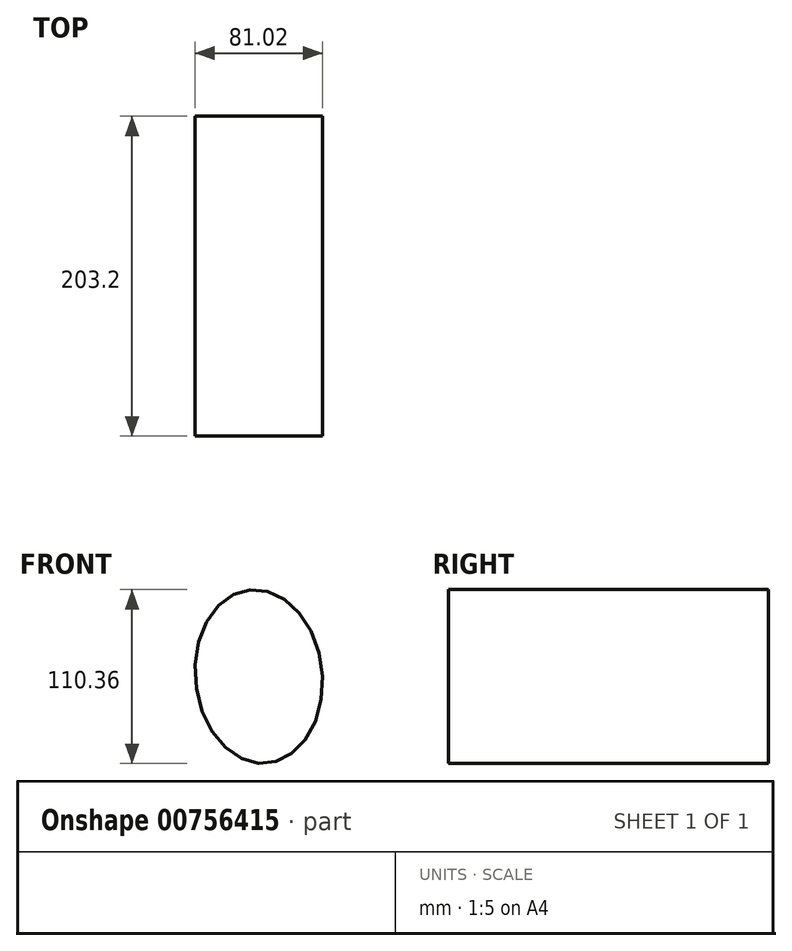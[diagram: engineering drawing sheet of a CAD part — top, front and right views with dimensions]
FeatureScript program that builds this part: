
annotation { "Feature Type Name" : "Feature", "Feature Type Description" : "" }
export const myFeature = defineFeature(function(context is Context, id is Id, definition is map)
    precondition{}
    {
        {
            var Q0;
            Q0=qCreatedBy(makeId("Front.planeOp"),FACE);
            var sketch = newSketch(context, id + "F0", { "sketchPlane" : qUnion([Q0])});
            skEllipse(sketch, "E0", {"center": v(0, 0) * mm, "majorRadius": 55.3 * mm, "minorRadius": 40.34 * mm, "majorAxis": v(-0.1, 1)});
            skSolve(sketch);
        }
        {
            var Q0;
            Q0=makeQuery(id+"F0.imprint","IMPRINT",FACE,{"disambiguationData":[TD([[makeQuery(id+"F0.imprint","IMPRINT",EDGE,{"derivedFrom":sQuery(id+"F0.wireOp",EDGE,"E0")}),1.0]])]});
            extrude(context, id + "F1", {"entities" : qUnion([Q0]), "endBound" : BoundingType.SYMMETRIC, "depth" : 203.2 * mm, "offsetDistance" : 25.4 * mm});
        }
    });
